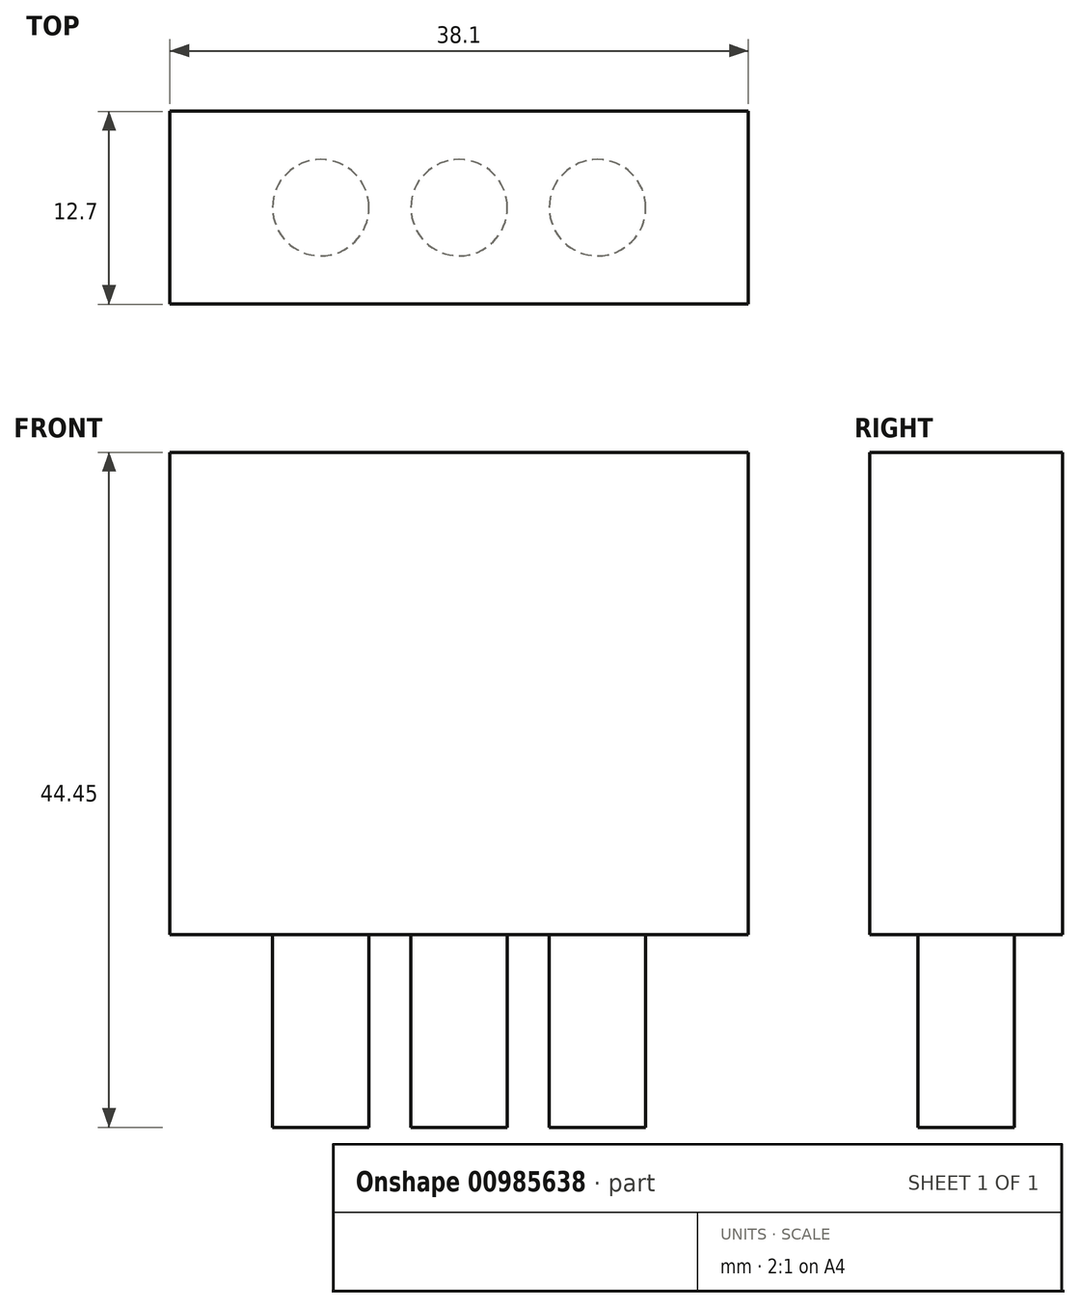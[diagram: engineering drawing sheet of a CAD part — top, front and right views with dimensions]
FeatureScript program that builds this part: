
annotation { "Feature Type Name" : "Feature", "Feature Type Description" : "" }
export const myFeature = defineFeature(function(context is Context, id is Id, definition is map)
    precondition{}
    {
        {
            var Q0;
            Q0=qCreatedBy(makeId("Top.planeOp"),FACE);
            var sketch = newSketch(context, id + "F0", { "sketchPlane" : qUnion([Q0])});
            skLineSegment(sketch, "E0.bottom", {"start": v(-15.84, 7.44) * mm, "end": v(22.26, 7.44) * mm});
            skLineSegment(sketch, "E0.top", {"start": v(-15.84, -5.26) * mm, "end": v(22.26, -5.26) * mm});
            skLineSegment(sketch, "E0.left", {"start": v(-15.84, 7.44) * mm, "end": v(-15.84, -5.26) * mm});
            skLineSegment(sketch, "E0.right", {"start": v(22.26, 7.44) * mm, "end": v(22.26, -5.26) * mm});
            skSolve(sketch);
        }
        {
            var Q0;
            Q0 = qSketchRegion(id + "F0", true);
            extrude(context, id + "F1", {"entities" : qUnion([Q0]), "depth" : 6.35 * mm, "offsetDistance" : 25.4 * mm});
        }
        {
            var Q0;
            Q0=makeQuery(id+"F1.opExtrude","CAP_FACE",FACE,{"disambiguationData":[OSD([sQuery(id+"F0.wireOp",EDGE,"E0.bottom"),sQuery(id+"F0.wireOp",EDGE,"E0.top"),sQuery(id+"F0.wireOp",EDGE,"E0.left"),sQuery(id+"F0.wireOp",EDGE,"E0.right")])],"isStart":false});
            var sketch = newSketch(context, id + "F2", { "sketchPlane" : qUnion([Q0])});
            skLineSegment(sketch, "E1.bottom", {"start": v(-15.84, 7.44) * mm, "end": v(22.26, 7.44) * mm});
            skLineSegment(sketch, "E1.top", {"start": v(-15.84, -5.26) * mm, "end": v(22.26, -5.26) * mm});
            skLineSegment(sketch, "E1.left", {"start": v(-15.84, 7.44) * mm, "end": v(-15.84, -5.26) * mm});
            skLineSegment(sketch, "E1.right", {"start": v(22.26, 7.44) * mm, "end": v(22.26, -5.26) * mm});
            skSolve(sketch);
        }
        {
            var Q0;
            Q0 = qSketchRegion(id + "F2", true);
            extrude(context, id + "F3", {"entities" : qUnion([Q0]), "operationType" : NewBodyOperationType.ADD, "depth" : 38.1 * mm, "offsetDistance" : 25.4 * mm});
        }
        {
            var Q0;
            Q0=makeQuery(id+"F1.opExtrude","CAP_FACE",FACE,{"disambiguationData":[OSD([sQuery(id+"F0.wireOp",EDGE,"E0.bottom"),sQuery(id+"F0.wireOp",EDGE,"E0.top"),sQuery(id+"F0.wireOp",EDGE,"E0.left"),sQuery(id+"F0.wireOp",EDGE,"E0.right")])],"isStart":true});
            var sketch = newSketch(context, id + "F4", { "sketchPlane" : qUnion([Q0])});
            skCircle(sketch, "E2", {"center": v(-5.9, -1.1) * mm, "radius": 3.18 * mm});
            skCircle(sketch, "E3", {"center": v(3.21, -1.1) * mm, "radius": 3.18 * mm});
            skCircle(sketch, "E4", {"center": v(12.33, -1.1) * mm, "radius": 3.18 * mm});
            skLineSegment(sketch, "E5.bottom", {"start": v(-15.84, 5.26) * mm, "end": v(22.26, 5.26) * mm});
            skLineSegment(sketch, "E5.top", {"start": v(-15.84, -7.44) * mm, "end": v(22.26, -7.44) * mm});
            skLineSegment(sketch, "E5.left", {"start": v(-15.84, 5.26) * mm, "end": v(-15.84, -7.44) * mm});
            skLineSegment(sketch, "E5.right", {"start": v(22.26, 5.26) * mm, "end": v(22.26, -7.44) * mm});
            skSolve(sketch);
        }
        {
            var Q0;
            Q0 = qSketchRegion(id + "F4", true);
            extrude(context, id + "F5", {"entities" : qUnion([Q0]), "operationType" : NewBodyOperationType.REMOVE, "oppositeDirection" : true, "depth" : 12.7 * mm, "offsetDistance" : 25.4 * mm});
        }
    });
